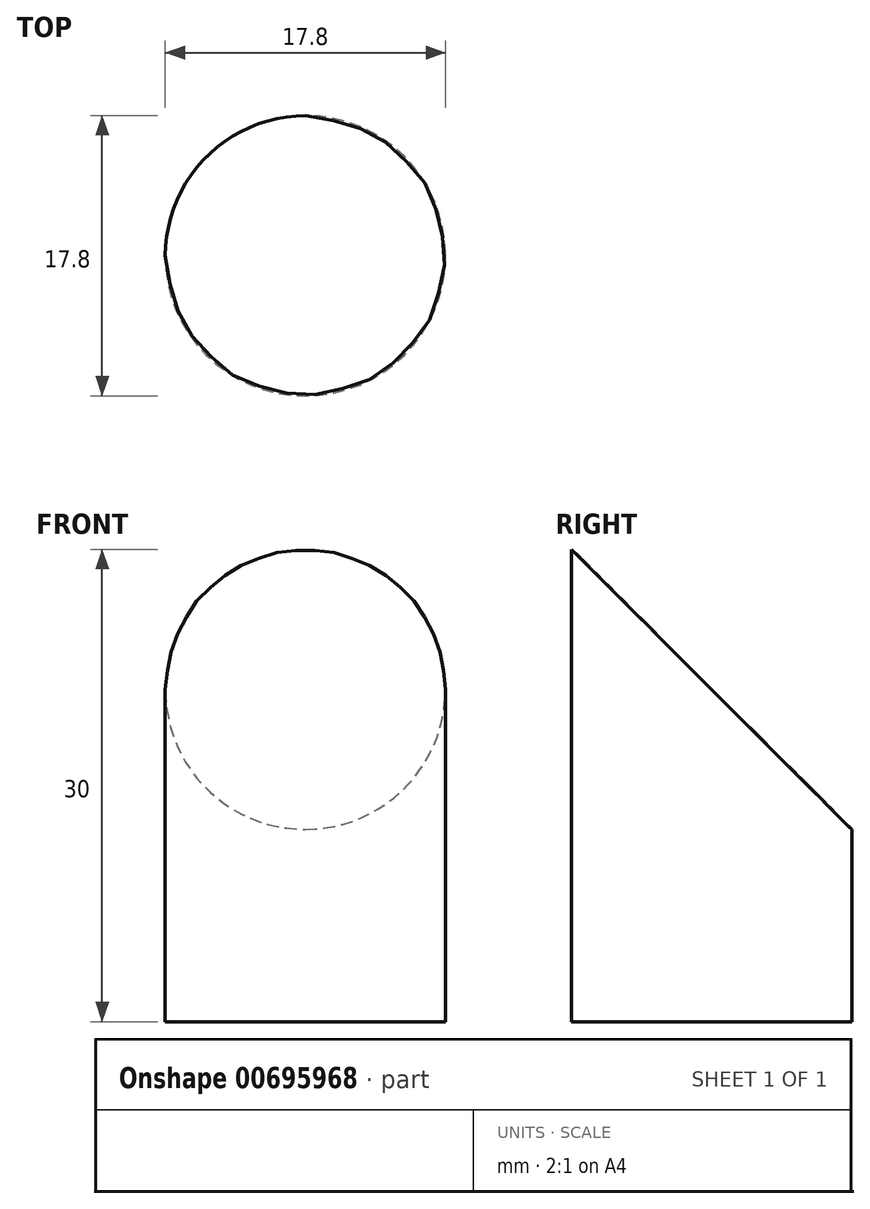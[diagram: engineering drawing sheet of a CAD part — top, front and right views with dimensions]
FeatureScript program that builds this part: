
annotation { "Feature Type Name" : "Feature", "Feature Type Description" : "" }
export const myFeature = defineFeature(function(context is Context, id is Id, definition is map)
    precondition{}
    {
        {
            var Q0;
            Q0=qCreatedBy(makeId("Front.planeOp"),FACE);
            var sketch = newSketch(context, id + "F0", { "sketchPlane" : qUnion([Q0])});
            skLineSegment(sketch, "E0.bottom", {"start": v(0, 0) * mm, "end": v(8.9, 0) * mm});
            skLineSegment(sketch, "E0.top", {"start": v(0, 30) * mm, "end": v(8.9, 30) * mm});
            skLineSegment(sketch, "E0.left", {"start": v(0, 0) * mm, "end": v(0, 30) * mm});
            skLineSegment(sketch, "E0.right", {"start": v(8.9, 0) * mm, "end": v(8.9, 30) * mm});
            skSolve(sketch);
        }
        {
            var Q0;
            Q0=makeQuery(id+"F0.imprint","IMPRINT",FACE,{"disambiguationData":[TD([[makeQuery(id+"F0.imprint","IMPRINT",EDGE,{"derivedFrom":sQuery(id+"F0.wireOp",EDGE,"E0.bottom")}),1.0]])]});
            var Q1;
            Q1=sQuery(id+"F0.wireOp",EDGE,"E0.left");
            revolve(context, id + "F1", {"entities" : qUnion([Q0]), "axis" : qUnion([Q1]), "revolveType" : RevolveType.FULL});
        }
        {
            var Q0;
            Q0=qCreatedBy(makeId("Right.planeOp"),FACE);
            var sketch = newSketch(context, id + "F2", { "sketchPlane" : qUnion([Q0])});
            skLineSegment(sketch, "E1.0", {"start": v(8.9, 30) * mm, "end": v(-8.9, 30) * mm});
            skLineSegment(sketch, "E2", {"start": v(8.9, 30) * mm, "end": v(8.9, -5.6) * mm});
            skLineSegment(sketch, "E3", {"start": v(-8.9, 0) * mm, "end": v(-8.9, 30) * mm});
            skLineSegment(sketch, "E4", {"start": v(-8.9, 0) * mm, "end": v(-8.9, 30) * mm, "construction": true});
            skLineSegment(sketch, "E5", {"start": v(8.9, 30) * mm, "end": v(8.9, 0) * mm, "construction": true});
            skLineSegment(sketch, "E6", {"start": v(-8.9, 30) * mm, "end": v(8.9, 12.2) * mm});
            skLineSegment(sketch, "E7", {"start": v(8.9, 12.2) * mm, "end": v(8.9, 30) * mm});
            skSolve(sketch);
        }
        {
            var Q0;
            Q0 = qSketchRegion(id + "F2", true);
            extrude(context, id + "F3", {"entities" : qUnion([Q0]), "operationType" : NewBodyOperationType.REMOVE, "endBound" : BoundingType.SYMMETRIC, "oppositeDirection" : true, "depth" : 25 * mm, "offsetDistance" : 25 * mm});
        }
    });
